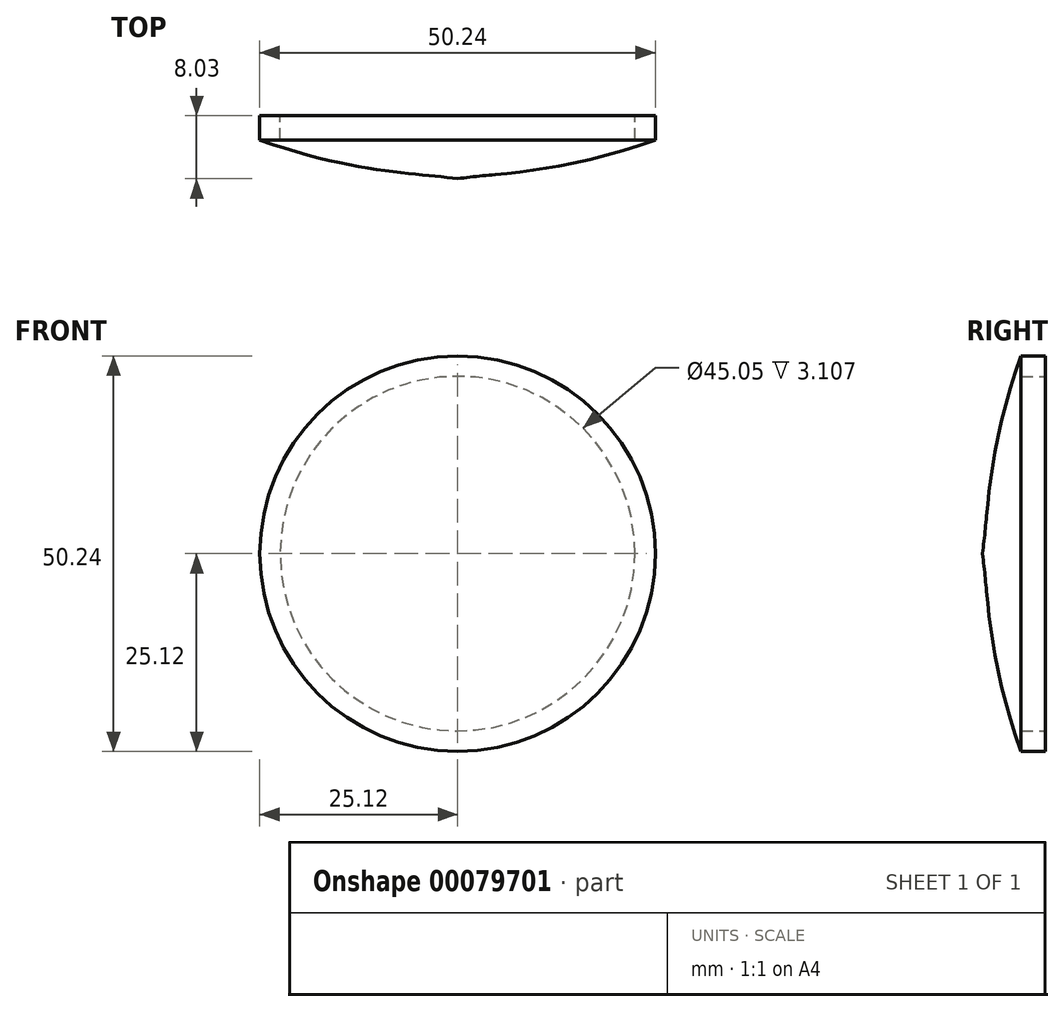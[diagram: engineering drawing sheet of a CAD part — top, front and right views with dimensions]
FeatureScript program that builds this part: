
annotation { "Feature Type Name" : "Feature", "Feature Type Description" : "" }
export const myFeature = defineFeature(function(context is Context, id is Id, definition is map)
    precondition{}
    {
        {
            var Q0;
            Q0=qCreatedBy(makeId("Top.planeOp"),FACE);
            var sketch = newSketch(context, id + "F0", { "sketchPlane" : qUnion([Q0])});
            skLineSegment(sketch, "E0", {"start": v(0, 0) * mm, "end": v(-22.53, 0) * mm});
            skLineSegment(sketch, "E1", {"start": v(-22.53, 0) * mm, "end": v(-22.53, 3.1) * mm});
            skLineSegment(sketch, "E2", {"start": v(-22.53, 3.1) * mm, "end": v(-25.12, 3.1) * mm});
            skLineSegment(sketch, "E3", {"start": v(-25.12, 3.1) * mm, "end": v(-25.12, 0) * mm});
            skLineSegment(sketch, "E4", {"start": v(0, 0) * mm, "end": v(0, -4.92) * mm});
            skFitSpline(sketch, "E5", {"points": [v(-25.12, 0) * mm, v(0, -4.92) * mm], "startDerivative": vector(37.29, -13.2) * mm, "endDerivative": vector(14.76, -2.33) * mm});
            skSolve(sketch);
        }
        {
            var Q0;
            Q0 = qSketchRegion(id + "F0", true);
            var Q1;
            Q1=sQuery(id+"F0.wireOp",EDGE,"E4");
            revolve(context, id + "F1", {"entities" : qUnion([Q0]), "axis" : qUnion([Q1]), "revolveType" : RevolveType.FULL});
        }
    });
